# Revit family: PELA-850-L30
name_source: partatom
category: Lighting Fixtures
units: mm (PartAtom-declared; Revit-internal decimal feet)

## family parameters
Cut with Voids When Loaded = No
Host = Face
Light Source = Yes
OmniClass Number = 23.80.70.11.14.17
OmniClass Title = Direct/Indirect
Part Type = Normal
Room Calculation Point = No
Round Connector Dimension = Use Diameter
Shared = Yes

## types (1)
- PELA-850-L30
    Additional Material Finish = Paint - Matte White
    Apparent Load = 227 VA
    Assembly Code = D5020200
    Available Finish Options = Available in Matte White
    Brand = Columbia Lighting
    Color Filter = 16777215
    Color Rendering Index = 80 CRI
    Controller = Please Refer to the Product Spec Sheet for Control Options
    Default Elevation = 48 "
    Description = The PELA is a compact high bay fixture with many options available from high lumen packages to switchable lumens as well as NX Controls.
    Dimming Lamp Color Temperature Shift = <None>
    Distribution Patterns = None
    Emit Shape Visible in Rendering = No
    Emit from Rectangle Length = 9 "
    Emit from Rectangle Width = 13 "
    Features = Ideal for high bay industrial and commercial buildings
Lumen packages from 9,000-48,000
Integrated emergency battery backup
Available with NX Connect integrated controls
    Housing Material = Paint - Matte White
    Installation and Service URL = https://cdn.currentlighting.com
    Lamp = LED
    Lens Material Finish = White Glass
    Load Classification = Lighting
    Manufacturer = Current Lighting
    Model = PELA-850-L30
    Mounting = Please Refer to the Product Spec Sheet for Mounting Options
    Optical Code = B
    Photometric Web File = PELA-850-L30-B-xxx_120-277V.IES
    Photometric Web Link = https://www.currentlighting.com
    Photometry Note = Please load ies file listed under Photometric Web File for accurate rendering.
    Power Factor = 1
    Product Documentation Link = https://cdn.currentlighting.com
    Product Page URL = https://www.currentlighting.com
    Tilt Angle = -90.00°
    Type Comments = Light Fixture
    URL = www.currentlighting.com
    Version = 2021 V 1.2
    Voltage = 120 V
    Voltage Comments = 120-277;347;480
    Warranty = 5 year limited
    Wattage Comments = 49 - 380 W

## geometry (parser evidence)
native form markers: Sweep x1
no freeform markers — native parametric forms only
